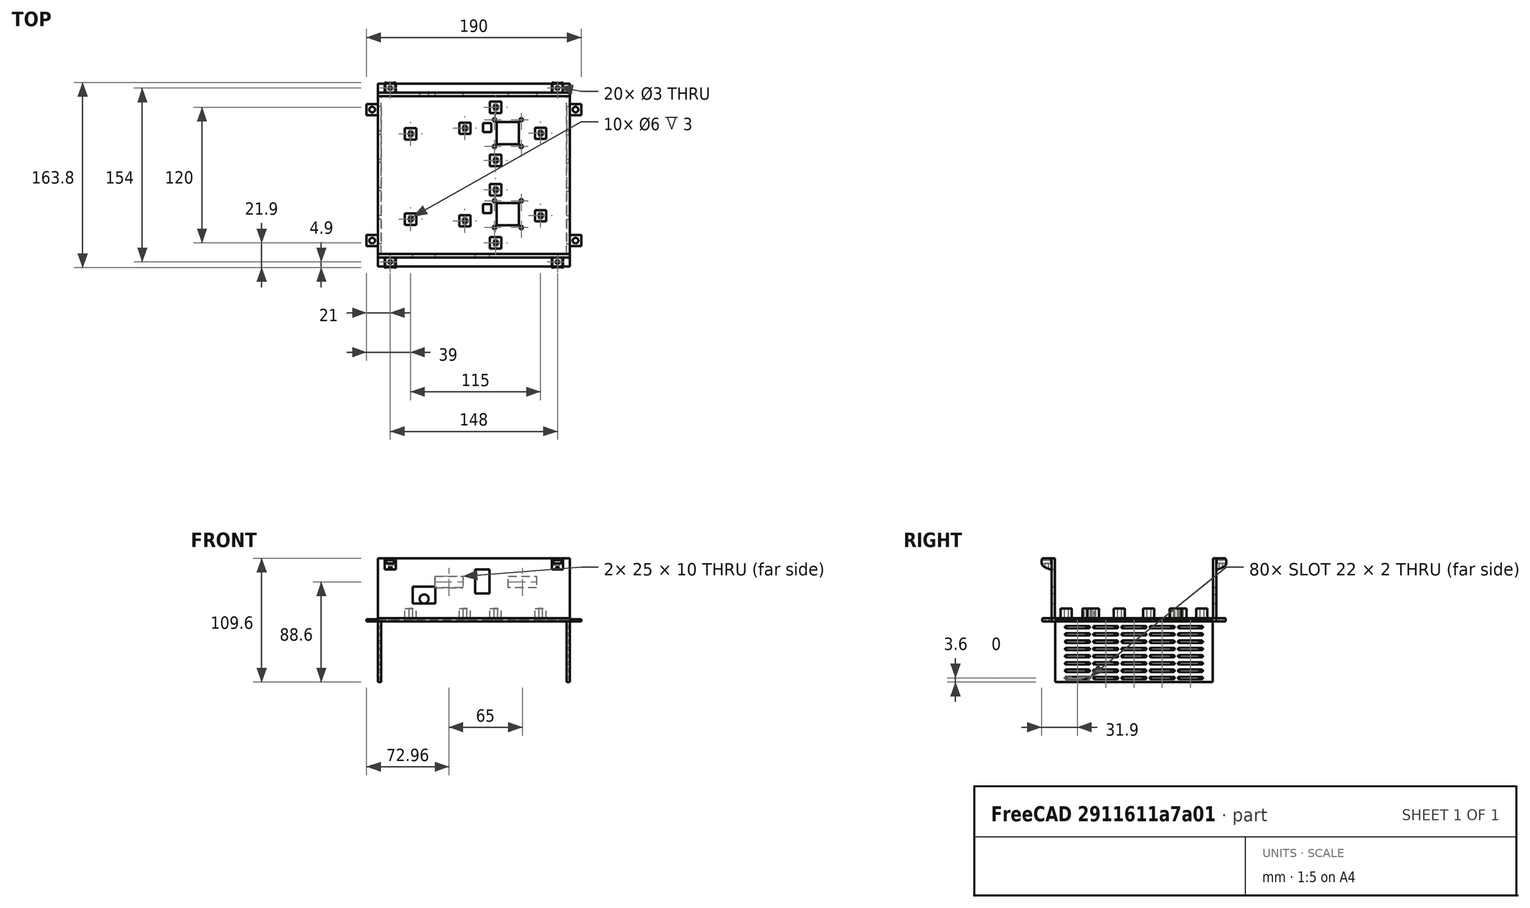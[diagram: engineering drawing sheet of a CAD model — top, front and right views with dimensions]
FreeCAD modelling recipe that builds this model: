
FCSTD DOCUMENT  (FreeCAD 0.21R33771 (Git))
Label: jrobot-electronics-parts
License: All rights reserved
LicenseURL: http://en.wikipedia.org/wiki/All_rights_reserved
objects: PartDesign::CoordinateSystem×24, Sketcher::SketchObject×16, PartDesign::Pocket×7, PartDesign::Pad×5, PartDesign::Mirrored×3, App::DocumentObjectGroup×3, PartDesign::MultiTransform×2, PartDesign::Body×2, App::Part×2, PartDesign::LinearPattern×2, PartDesign::AdditiveLoft×1
note: 75 computed .brp shape members not serialized (recipe doc carries the construction recipe); baked Part::Feature solids carry a one-line shape summary decoded from their .brp

FEATURE [PartDesign::CoordinateSystem] LCS_ElectronicsBox_Lid
  AttacherType = Attacher::AttachEngine3D
  Placement = pos=(0,0,56) rot=(0,0,1;0rad)
FEATURE [PartDesign::CoordinateSystem] LCS_Origin006  label="LCS_ElectronicsBox_Origin"
  AttacherType = Attacher::AttachEngine3D
  MapMode = 2
  Support = -> [X_Axis026]
FEATURE [Sketcher::SketchObject] Sketch034  label="S_ElectronicsBox_HoleLocations"
  FullyConstrained = true
  Support = -> [XY_Plane027]
  sketch-geometry (27):
    g0: LineSegment StartX=-85 StartY=73 StartZ=0 EndX=-85 EndY=-73 EndZ=0
    g1: LineSegment StartX=-85 StartY=-73 StartZ=0 EndX=85 EndY=-73 EndZ=0
    g2: LineSegment StartX=85 StartY=-73 StartZ=0 EndX=85 EndY=73 EndZ=0
    g3: LineSegment StartX=85 StartY=73 StartZ=0 EndX=-85 EndY=73 EndZ=0
    g4: GeomPoint X=0 Y=0 Z=0
    g5: LineSegment StartX=5 StartY=63 StartZ=0 EndX=74 EndY=63 EndZ=0
    g6: LineSegment StartX=74 StartY=63 StartZ=0 EndX=74 EndY=10 EndZ=0
    g7: LineSegment StartX=74 StartY=10 StartZ=0 EndX=5 EndY=10 EndZ=0
    g8: LineSegment StartX=5 StartY=10 StartZ=0 EndX=5 EndY=63 EndZ=0
    g9: LineSegment StartX=5 StartY=-10 StartZ=0 EndX=74 EndY=-10 EndZ=0
    g10: LineSegment StartX=74 StartY=-10 StartZ=0 EndX=74 EndY=-63 EndZ=0
    g11: LineSegment StartX=74 StartY=-63 StartZ=0 EndX=5 EndY=-63 EndZ=0
    g12: LineSegment StartX=5 StartY=-63 StartZ=0 EndX=5 EndY=-10 EndZ=0
    g13: LineSegment StartX=-60 StartY=54 StartZ=0 EndX=-5 EndY=54 EndZ=0
    g14: LineSegment StartX=-5 StartY=54 StartZ=0 EndX=-5 EndY=-54 EndZ=0
    g15: LineSegment StartX=-5 StartY=-54 StartZ=0 EndX=-60 EndY=-54 EndZ=0
    g16: LineSegment StartX=-60 StartY=-54 StartZ=0 EndX=-60 EndY=54 EndZ=0
    g17: GeomPoint X=19.25 Y=60 Z=0
    g18: GeomPoint X=19.25 Y=13 Z=0
    g19: GeomPoint X=19.25 Y=-60 Z=0
    g20: GeomPoint X=19.25 Y=-13 Z=0
    g21: GeomPoint X=59 Y=37 Z=0
    g22: GeomPoint X=59 Y=-36 Z=0
    g23: GeomPoint X=-56 Y=36.5 Z=0
    g24: GeomPoint X=-8 Y=41.5 Z=0
    g25: GeomPoint X=-56 Y=-39 Z=0
    g26: GeomPoint X=-8 Y=-40.5 Z=0
  constraints (70):
    c: Coincident(g0,g1)
    c: Coincident(g1,g2)
    c: Coincident(g2,g3)
    c: Coincident(g3,g0)
    c: Horizontal(g1)
    c: Horizontal(g3)
    c: Vertical(g0)
    c: Vertical(g2)
    c: Symmetric(g1,g0,g4)
    c: Coincident(g4,g-1)
    c: Coincident(g5,g6)
    c: Coincident(g6,g7)
    c: Coincident(g7,g8)
    c: Coincident(g8,g5)
    c: Horizontal(g5)
    c: Horizontal(g7)
    c: Vertical(g6)
    c: Vertical(g8)
    c: DistanceX(g5,g5) = 69
    c: DistanceY(g6,g6) = 53
    c: Coincident(g9,g10)
    c: Coincident(g10,g11)
    c: Coincident(g11,g12)
    c: Coincident(g12,g9)
    c: Horizontal(g9)
    c: Horizontal(g11)
    c: Vertical(g10)
    c: Vertical(g12)
    c: Equal(g7,g9)
    c: Equal(g6,g10)
    c: Vertical(g7,g9)
    c: DistanceY(g9,g7) = 20
    c: DistanceY(g4,g7) = 10
    c: Coincident(g13,g14)
    c: Coincident(g14,g15)
    c: Coincident(g15,g16)
    c: Coincident(g16,g13)
    c: Horizontal(g13)
    c: Horizontal(g15)
    c: Vertical(g16)
    c: DistanceX(g13,g13) = 55
    c: DistanceY(g14,g14) = 108
    c: DistanceX(g13,g4) = 5
    c: DistanceX(g4,g5) = 5
    c: Symmetric(g13,g14,g-1)
    c: DistanceX(g0,g13) = 25
    c: DistanceY(g17,g5) = 3
    c: DistanceY(g7,g18) = 3
    c: DistanceX(g7,g18) = 14.25
    c: Vertical(g18,g17)
    c: DistanceX(g11,g19) = 14.25
    c: DistanceY(g11,g19) = 3
    c: DistanceY(g20,g9) = 3
    c: Vertical(g20,g19)
    c: Vertical(g21,g22)
    c: DistanceY(g21,g5) = 26
    c: DistanceY(g22,g9) = 26
    c: DistanceY(g2,g2) = 146
    c: DistanceY(g25,g23) = 75.5
    c: DistanceX(g15,g25) = 4
    c: DistanceY(g15,g25) = 15
    c: Vertical(g23,g25)
    c: DistanceY(g14,g26) = 13.5
    c: DistanceX(g26,g14) = 3
    c: Vertical(g24,g26)
    c: DistanceY(g26,g24) = 82
    c: DistanceX(g22,g10) = 15
    c: DistanceY(g18,g17) = 47  'HoleYSeparation1'
    c: DistanceY(g18,g21) = 24  'HoleYSeparation0'
    c: DistanceX(g18,g21) = 39.75  'HoleXSeparation'
FEATURE [Sketcher::SketchObject] Sketch033  label="S_ElectronicsBox_Base"
  ExternalGeometry = -> [Sketch034]
  FullyConstrained = true
  MapMode = 5
  Support = -> [XY_Plane027]
  sketch-geometry (24):
    g0: LineSegment StartX=-85 StartY=73 StartZ=0 EndX=-85 EndY=63 EndZ=0
    g1: LineSegment StartX=-85 StartY=-73 StartZ=0 EndX=85 EndY=-73 EndZ=0
    g2: LineSegment StartX=85 StartY=73 StartZ=0 EndX=-85 EndY=73 EndZ=0
    g3: LineSegment StartX=-85 StartY=63 StartZ=0 EndX=-95 EndY=63 EndZ=0
    g4: LineSegment StartX=-95 StartY=63 StartZ=0 EndX=-95 EndY=53 EndZ=0
    g5: LineSegment StartX=-95 StartY=53 StartZ=0 EndX=-85 EndY=53 EndZ=0
    g6: LineSegment StartX=-85 StartY=-53 StartZ=0 EndX=-95 EndY=-53 EndZ=0
    g7: LineSegment StartX=-95 StartY=-53 StartZ=0 EndX=-95 EndY=-63 EndZ=0
    g8: LineSegment StartX=-95 StartY=-63 StartZ=0 EndX=-85 EndY=-63 EndZ=0
    g9: LineSegment StartX=85 StartY=63 StartZ=0 EndX=95 EndY=63 EndZ=0
    g10: LineSegment StartX=95 StartY=63 StartZ=0 EndX=95 EndY=53 EndZ=0
    g11: LineSegment StartX=95 StartY=53 StartZ=0 EndX=85 EndY=53 EndZ=0
    g12: LineSegment StartX=85 StartY=-53 StartZ=0 EndX=95 EndY=-53 EndZ=0
    g13: LineSegment StartX=95 StartY=-53 StartZ=0 EndX=95 EndY=-63 EndZ=0
    g14: LineSegment StartX=95 StartY=-63 StartZ=0 EndX=85 EndY=-63 EndZ=0
    g15: LineSegment StartX=-85 StartY=-63 StartZ=0 EndX=-85 EndY=-73 EndZ=0
    g16: LineSegment StartX=-85 StartY=53 StartZ=0 EndX=-85 EndY=-53 EndZ=0
    g17: LineSegment StartX=85 StartY=-73 StartZ=0 EndX=85 EndY=-63 EndZ=0
    g18: LineSegment StartX=85 StartY=-53 StartZ=0 EndX=85 EndY=53 EndZ=0
    g19: LineSegment StartX=85 StartY=63 StartZ=0 EndX=85 EndY=73 EndZ=0
    g20: Circle CenterX=-90 CenterY=-58 CenterZ=0 NormalX=0 NormalY=0 NormalZ=1 AngleXU=0 Radius=2.5
    g21: Circle CenterX=-90 CenterY=58 CenterZ=0 NormalX=0 NormalY=0 NormalZ=1 AngleXU=0 Radius=2.5
    g22: Circle CenterX=90 CenterY=58 CenterZ=0 NormalX=0 NormalY=0 NormalZ=1 AngleXU=0 Radius=2.5
    g23: Circle CenterX=90 CenterY=-58 CenterZ=0 NormalX=0 NormalY=0 NormalZ=1 AngleXU=0 Radius=2.5
  constraints (70):
    c: Coincident(g2,g0)
    c: Horizontal(g1)
    c: Horizontal(g2)
    c: Vertical(g0)
    c: Symmetric(g1,g0,g-1)
    c: Coincident(g0,g-3)
    c: Coincident(g3,g4)
    c: Coincident(g4,g5)
    c: Horizontal(g3)
    c: Horizontal(g5)
    c: Vertical(g4)
    c: Coincident(g6,g7)
    c: Coincident(g7,g8)
    c: Horizontal(g6)
    c: Horizontal(g8)
    c: Vertical(g7)
    c: PointOnObject(g6,g0)
    c: Coincident(g9,g10)
    c: Coincident(g10,g11)
    c: Horizontal(g9)
    c: Horizontal(g11)
    c: Vertical(g10)
    c: Coincident(g12,g13)
    c: Coincident(g13,g14)
    c: Horizontal(g12)
    c: Horizontal(g14)
    c: Vertical(g13)
    c: Horizontal(g3,g9)
    c: Horizontal(g5,g11)
    c: Horizontal(g12,g6)
    c: Horizontal(g8,g14)
    c: DistanceY(g7,g7) = 10
    c: Equal(g7,g4)
    c: DistanceX(g8,g8) = 10
    c: Equal(g8,g14)
    c: Vertical(g10,g12)
    c: Equal(g5,g8)
    c: DistanceY(g1,g8) = 10
    c: DistanceY(g3,g0) = 10
    c: Coincident(g0,g3)
    c: Vertical(g5,g0)
    c: Coincident(g15,g8)
    c: Coincident(g15,g1)
    c: Vertical(g15)
    c: Vertical(g6,g1)
    c: Coincident(g16,g5)
    c: Coincident(g16,g6)
    c: Coincident(g17,g1)
    c: Coincident(g17,g14)
    c: Vertical(g17)
    c: Coincident(g18,g12)
    c: Coincident(g18,g11)
    c: Vertical(g18)
    c: Coincident(g19,g9)
    c: Coincident(g19,g2)
    c: Vertical(g19)
    c: Vertical(g18,g9)
    c: DistanceX(g0,g2) = 170
    c: Diameter(g20) = 5
    c: DistanceX(g20,g6) = 5
    c: DistanceY(g8,g20) = 5
    c: DistanceY(g21,g0) = 5
    c: DistanceX(g21,g0) = 5
    c: Diameter(g21) = 5
    c: Diameter(g23) = 5
    c: Diameter(g22) = 5
    c: DistanceX(g9,g22) = 5
    c: Horizontal(g21,g22)
    c: Horizontal(g20,g23)
    c: Vertical(g23,g22)
FEATURE [PartDesign::Pad] Pad016  label="PAD_ElectronicsBox_Base"
  Direction = (0,0,1)
  Length = 2
  Length2 = 10
  Profile = -> Sketch033
  ReferenceAxis = -> Sketch033 [N_Axis]
  Type = 0
FEATURE [Sketcher::SketchObject] Sketch035  label="S_ElectronicsBox_HolePads"
  ExternalGeometry = -> [Sketch034]
  FullyConstrained = true
  MapMode = 5
  Placement = pos=(0,0,1.5) rot=(0,0,1;0rad)
  sketch-geometry (50):
    g0: LineSegment StartX=-61 StartY=41.5 StartZ=0 EndX=-61 EndY=31.5 EndZ=0
    g1: LineSegment StartX=-61 StartY=31.5 StartZ=0 EndX=-51 EndY=31.5 EndZ=0
    g2: LineSegment StartX=-51 StartY=31.5 StartZ=0 EndX=-51 EndY=41.5 EndZ=0
    g3: LineSegment StartX=-51 StartY=41.5 StartZ=0 EndX=-61 EndY=41.5 EndZ=0
    g4: GeomPoint X=-56 Y=36.5 Z=0
    g5: LineSegment StartX=-61 StartY=-34 StartZ=0 EndX=-61 EndY=-44 EndZ=0
    g6: LineSegment StartX=-61 StartY=-44 StartZ=0 EndX=-51 EndY=-44 EndZ=0
    g7: LineSegment StartX=-51 StartY=-44 StartZ=0 EndX=-51 EndY=-34 EndZ=0
    g8: LineSegment StartX=-51 StartY=-34 StartZ=0 EndX=-61 EndY=-34 EndZ=0
    g9: GeomPoint X=-56 Y=-39 Z=0
    g10: LineSegment StartX=-13 StartY=46.5 StartZ=0 EndX=-13 EndY=36.5 EndZ=0
    g11: LineSegment StartX=-13 StartY=36.5 StartZ=0 EndX=-3 EndY=36.5 EndZ=0
    g12: LineSegment StartX=-3 StartY=36.5 StartZ=0 EndX=-3 EndY=46.5 EndZ=0
    g13: LineSegment StartX=-3 StartY=46.5 StartZ=0 EndX=-13 EndY=46.5 EndZ=0
    g14: GeomPoint X=-8 Y=41.5 Z=0
    g15: LineSegment StartX=-13 StartY=-35.5 StartZ=0 EndX=-13 EndY=-45.5 EndZ=0
    g16: LineSegment StartX=-13 StartY=-45.5 StartZ=0 EndX=-3 EndY=-45.5 EndZ=0
    g17: LineSegment StartX=-3 StartY=-45.5 StartZ=0 EndX=-3 EndY=-35.5 EndZ=0
    g18: LineSegment StartX=-3 StartY=-35.5 StartZ=0 EndX=-13 EndY=-35.5 EndZ=0
    g19: GeomPoint X=-8 Y=-40.5 Z=0
    g20: LineSegment StartX=14.25 StartY=65 StartZ=0 EndX=14.25 EndY=55 EndZ=0
    g21: LineSegment StartX=14.25 StartY=55 StartZ=0 EndX=24.25 EndY=55 EndZ=0
    g22: LineSegment StartX=24.25 StartY=55 StartZ=0 EndX=24.25 EndY=65 EndZ=0
    g23: LineSegment StartX=24.25 StartY=65 StartZ=0 EndX=14.25 EndY=65 EndZ=0
    g24: GeomPoint X=19.25 Y=60 Z=0
    g25: LineSegment StartX=54 StartY=42 StartZ=0 EndX=54 EndY=32 EndZ=0
    g26: LineSegment StartX=54 StartY=32 StartZ=0 EndX=64 EndY=32 EndZ=0
    g27: LineSegment StartX=64 StartY=32 StartZ=0 EndX=64 EndY=42 EndZ=0
    g28: LineSegment StartX=64 StartY=42 StartZ=0 EndX=54 EndY=42 EndZ=0
    g29: GeomPoint X=59 Y=37 Z=0
    g30: LineSegment StartX=14.25 StartY=18 StartZ=0 EndX=14.25 EndY=8 EndZ=0
    g31: LineSegment StartX=14.25 StartY=8 StartZ=0 EndX=24.25 EndY=8 EndZ=0
    g32: LineSegment StartX=24.25 StartY=8 StartZ=0 EndX=24.25 EndY=18 EndZ=0
    g33: LineSegment StartX=24.25 StartY=18 StartZ=0 EndX=14.25 EndY=18 EndZ=0
    g34: GeomPoint X=19.25 Y=13 Z=0
    g35: LineSegment StartX=14.25 StartY=-8 StartZ=0 EndX=14.25 EndY=-18 EndZ=0
    g36: LineSegment StartX=14.25 StartY=-18 StartZ=0 EndX=24.25 EndY=-18 EndZ=0
    g37: LineSegment StartX=24.25 StartY=-18 StartZ=0 EndX=24.25 EndY=-8 EndZ=0
    g38: LineSegment StartX=24.25 StartY=-8 StartZ=0 EndX=14.25 EndY=-8 EndZ=0
    g39: GeomPoint X=19.25 Y=-13 Z=0
    g40: LineSegment StartX=54 StartY=-31 StartZ=0 EndX=54 EndY=-41 EndZ=0
    g41: LineSegment StartX=54 StartY=-41 StartZ=0 EndX=64 EndY=-41 EndZ=0
    g42: LineSegment StartX=64 StartY=-41 StartZ=0 EndX=64 EndY=-31 EndZ=0
    g43: LineSegment StartX=64 StartY=-31 StartZ=0 EndX=54 EndY=-31 EndZ=0
    g44: GeomPoint X=59 Y=-36 Z=0
    g45: LineSegment StartX=14.25 StartY=-55 StartZ=0 EndX=14.25 EndY=-65 EndZ=0
    g46: LineSegment StartX=14.25 StartY=-65 StartZ=0 EndX=24.25 EndY=-65 EndZ=0
    g47: LineSegment StartX=24.25 StartY=-65 StartZ=0 EndX=24.25 EndY=-55 EndZ=0
    g48: LineSegment StartX=24.25 StartY=-55 StartZ=0 EndX=14.25 EndY=-55 EndZ=0
    g49: GeomPoint X=19.25 Y=-60 Z=0
  constraints (120):
    c: Coincident(g0,g1)
    c: Coincident(g1,g2)
    c: Coincident(g2,g3)
    c: Coincident(g3,g0)
    c: Horizontal(g1)
    c: Horizontal(g3)
    c: Vertical(g0)
    c: Vertical(g2)
    c: Symmetric(g1,g0,g4)
    c: Coincident(g5,g6)
    c: Coincident(g6,g7)
    c: Coincident(g7,g8)
    c: Coincident(g8,g5)
    c: Horizontal(g6)
    c: Horizontal(g8)
    c: Vertical(g5)
    c: Vertical(g7)
    c: Symmetric(g6,g5,g9)
    c: Coincident(g10,g11)
    c: Coincident(g11,g12)
    c: Coincident(g12,g13)
    c: Coincident(g13,g10)
    c: Horizontal(g11)
    c: Horizontal(g13)
    c: Vertical(g10)
    c: Vertical(g12)
    c: Symmetric(g11,g10,g14)
    c: Coincident(g15,g16)
    c: Coincident(g16,g17)
    c: Coincident(g17,g18)
    c: Coincident(g18,g15)
    c: Horizontal(g16)
    c: Horizontal(g18)
    c: Vertical(g15)
    c: Vertical(g17)
    c: Symmetric(g16,g15,g19)
    c: Coincident(g20,g21)
    c: Coincident(g21,g22)
    c: Coincident(g22,g23)
    c: Coincident(g23,g20)
    c: Horizontal(g21)
    c: Horizontal(g23)
    c: Vertical(g20)
    c: Vertical(g22)
    c: Symmetric(g21,g20,g24)
    c: Coincident(g25,g26)
    c: Coincident(g26,g27)
    c: Coincident(g27,g28)
    c: Coincident(g28,g25)
    c: Horizontal(g26)
    c: Horizontal(g28)
    c: Vertical(g25)
    c: Vertical(g27)
    c: Symmetric(g26,g25,g29)
    c: Coincident(g30,g31)
    c: Coincident(g31,g32)
    c: Coincident(g32,g33)
    c: Coincident(g33,g30)
    c: Horizontal(g31)
    c: Horizontal(g33)
    c: Vertical(g30)
    c: Vertical(g32)
    c: Symmetric(g31,g30,g34)
    c: Coincident(g35,g36)
    c: Coincident(g36,g37)
    c: Coincident(g37,g38)
    c: Coincident(g38,g35)
    c: Horizontal(g36)
    c: Horizontal(g38)
    c: Vertical(g35)
    c: Vertical(g37)
    c: Symmetric(g36,g35,g39)
    c: Coincident(g40,g41)
    c: Coincident(g41,g42)
    c: Coincident(g42,g43)
    c: Coincident(g43,g40)
    c: Horizontal(g41)
    c: Horizontal(g43)
    c: Vertical(g40)
    c: Vertical(g42)
    c: Symmetric(g41,g40,g44)
    c: Coincident(g45,g46)
    c: Coincident(g46,g47)
    c: Coincident(g47,g48)
    c: Coincident(g48,g45)
    c: Horizontal(g46)
    c: Horizontal(g48)
    c: Vertical(g45)
    c: Vertical(g47)
    c: Symmetric(g46,g45,g49)
    c: Coincident(g4,g-3)
    c: Coincident(g9,g-12)
    c: Coincident(g19,g-9)
    c: Coincident(g14,g-4)
    c: Coincident(g24,g-11)
    c: Coincident(g29,g-6)
    c: Coincident(g34,g-5)
    c: Coincident(g39,g-10)
    c: Coincident(g44,g-7)
    c: Coincident(g49,g-8)
    c: Equal(g3,g2)
    c: Equal(g8,g7)
    c: Equal(g18,g17)
    c: Equal(g13,g12)
    c: Equal(g33,g32)
    c: Equal(g38,g37)
    c: Equal(g48,g47)
    c: Equal(g43,g42)
    c: Equal(g28,g27)
    c: Equal(g23,g22)
    c: Equal(g3,g8)
    c: Equal(g3,g13)
    c: Equal(g13,g23)
    c: Equal(g23,g28)
    c: Equal(g28,g33)
    c: Equal(g33,g38)
    c: Equal(g38,g48)
    c: Equal(g18,g8)
    c: Equal(g48,g43)
    c: DistanceX(g3,g3) = 10
FEATURE [Sketcher::SketchObject] Sketch036  label="S_ElectronicsBox_Holes"
  AttachmentOffset = pos=(2,0,0) rot=(0,0,1;0rad)
  ExternalGeometry = -> [Sketch034]
  FullyConstrained = true
  MapMode = 5
  Placement = pos=(2,0,0) rot=(1,0,0;3.14159rad)
  sketch-geometry (10):
    g0: Circle CenterX=-58 CenterY=39 CenterZ=0 NormalX=0 NormalY=0 NormalZ=1 AngleXU=0 Radius=1.75
    g1: Circle CenterX=-10 CenterY=40.5 CenterZ=0 NormalX=0 NormalY=0 NormalZ=1 AngleXU=0 Radius=1.75
    g2: Circle CenterX=-10 CenterY=-41.5 CenterZ=0 NormalX=0 NormalY=0 NormalZ=1 AngleXU=0 Radius=1.75
    g3: Circle CenterX=-58 CenterY=-36.5 CenterZ=0 NormalX=0 NormalY=0 NormalZ=1 AngleXU=0 Radius=1.75
    g4: Circle CenterX=17.25 CenterY=13 CenterZ=0 NormalX=0 NormalY=0 NormalZ=1 AngleXU=0 Radius=1.75
    g5: Circle CenterX=17.25 CenterY=60 CenterZ=0 NormalX=0 NormalY=0 NormalZ=1 AngleXU=0 Radius=1.75
    g6: Circle CenterX=57 CenterY=36 CenterZ=0 NormalX=0 NormalY=0 NormalZ=1 AngleXU=0 Radius=1.75
    g7: Circle CenterX=57 CenterY=-37 CenterZ=0 NormalX=0 NormalY=0 NormalZ=1 AngleXU=0 Radius=1.75
    g8: Circle CenterX=17.25 CenterY=-13 CenterZ=0 NormalX=0 NormalY=0 NormalZ=1 AngleXU=0 Radius=1.75
    g9: Circle CenterX=17.25 CenterY=-60 CenterZ=0 NormalX=0 NormalY=0 NormalZ=1 AngleXU=0 Radius=1.75
  constraints (20):
    c: Coincident(g0,g-3)
    c: Coincident(g1,g-4)
    c: Coincident(g2,g-5)
    c: Coincident(g3,g-6)
    c: Coincident(g4,g-12)
    c: Coincident(g5,g-11)
    c: Coincident(g6,g-10)
    c: Coincident(g7,g-9)
    c: Coincident(g8,g-8)
    c: Coincident(g9,g-7)
    c: Equal(g0,g1)
    c: Equal(g1,g2)
    c: Equal(g2,g3)
    c: Equal(g3,g8)
    c: Equal(g8,g9)
    c: Equal(g9,g7)
    c: Equal(g7,g4)
    c: Equal(g4,g6)
    c: Equal(g6,g5)
    c: Diameter(g0) = 3.5
FEATURE [Sketcher::SketchObject] Sketch037  label="S_ElectronicsBox_BoltIndent"
  ExternalGeometry = -> [Sketch034]
  FullyConstrained = true
  MapMode = 5
  Placement = pos=(0,0,0) rot=(1,0,0;3.14159rad)
  sketch-geometry (10):
    g0: Circle CenterX=-56 CenterY=39 CenterZ=0 NormalX=0 NormalY=0 NormalZ=1 AngleXU=0 Radius=3
    g1: Circle CenterX=-8 CenterY=40.5 CenterZ=0 NormalX=0 NormalY=0 NormalZ=1 AngleXU=0 Radius=3
    g2: Circle CenterX=-8 CenterY=-41.5 CenterZ=0 NormalX=0 NormalY=0 NormalZ=1 AngleXU=0 Radius=3
    g3: Circle CenterX=-56 CenterY=-36.5 CenterZ=0 NormalX=0 NormalY=0 NormalZ=1 AngleXU=0 Radius=3
    g4: Circle CenterX=19.25 CenterY=13 CenterZ=0 NormalX=0 NormalY=0 NormalZ=1 AngleXU=0 Radius=3
    g5: Circle CenterX=19.25 CenterY=60 CenterZ=0 NormalX=0 NormalY=0 NormalZ=1 AngleXU=0 Radius=3
    g6: Circle CenterX=59 CenterY=36 CenterZ=0 NormalX=0 NormalY=0 NormalZ=1 AngleXU=0 Radius=3
    g7: Circle CenterX=59 CenterY=-37 CenterZ=0 NormalX=0 NormalY=0 NormalZ=1 AngleXU=0 Radius=3
    g8: Circle CenterX=19.25 CenterY=-13 CenterZ=0 NormalX=0 NormalY=0 NormalZ=1 AngleXU=0 Radius=3
    g9: Circle CenterX=19.25 CenterY=-60 CenterZ=0 NormalX=0 NormalY=0 NormalZ=1 AngleXU=0 Radius=3
  constraints (20):
    c: Coincident(g0,g-3)
    c: Coincident(g1,g-4)
    c: Coincident(g2,g-5)
    c: Coincident(g3,g-6)
    c: Coincident(g4,g-12)
    c: Coincident(g5,g-11)
    c: Coincident(g6,g-10)
    c: Coincident(g7,g-9)
    c: Coincident(g8,g-8)
    c: Coincident(g9,g-7)
    c: Equal(g0,g1)
    c: Equal(g1,g2)
    c: Equal(g2,g3)
    c: Equal(g3,g8)
    c: Equal(g8,g9)
    c: Equal(g9,g7)
    c: Equal(g7,g4)
    c: Equal(g4,g6)
    c: Equal(g6,g5)
    c: Diameter(g0) = 6
FEATURE [Sketcher::SketchObject] Sketch038  label="S_ElectronicsBox_Switches"
  FullyConstrained = true
  MapMode = 5
  Placement = pos=(0,-73,0) rot=(1,0,0;1.5708rad)
  sketch-geometry (10):
    g0: LineSegment StartX=1.16 StartY=46 StartZ=0 EndX=13.66 EndY=46 EndZ=0
    g1: LineSegment StartX=13.66 StartY=46 StartZ=0 EndX=13.66 EndY=25 EndZ=0
    g2: LineSegment StartX=13.66 StartY=25 StartZ=0 EndX=1.16 EndY=25 EndZ=0
    g3: LineSegment StartX=1.16 StartY=25 StartZ=0 EndX=1.16 EndY=46 EndZ=0
    g4: LineSegment StartX=-54 StartY=31 StartZ=0 EndX=-34 EndY=31 EndZ=0
    g5: LineSegment StartX=-34 StartY=31 StartZ=0 EndX=-34 EndY=16 EndZ=0
    g6: LineSegment StartX=-34 StartY=16 StartZ=0 EndX=-54 EndY=16 EndZ=0
    g7: LineSegment StartX=-54 StartY=16 StartZ=0 EndX=-54 EndY=31 EndZ=0
    g8: GeomPoint X=-44 Y=23.5 Z=0
    g9: GeomPoint X=7.41 Y=35.5 Z=0
  constraints (30):
    c: Coincident(g0,g1)
    c: Coincident(g1,g2)
    c: Coincident(g2,g3)
    c: Coincident(g3,g0)
    c: Horizontal(g0)
    c: Horizontal(g2)
    c: Vertical(g1)
    c: Vertical(g3)
    c: DistanceX(g0,g0) = 12.5
    c: DistanceY(g3,g3) = 21
    c: Coincident(g4,g5)
    c: Coincident(g5,g6)
    c: Coincident(g6,g7)
    c: Coincident(g7,g4)
    c: Horizontal(g4)
    c: Horizontal(g6)
    c: Vertical(g5)
    c: Vertical(g7)
    c: DistanceY(g-1,g5) = 16
    c: DistanceY(g6,g4) = 15
    c: DistanceX(g4,g4) = 20
    c: DistanceX(g5,g-1) = 34
    c: DistanceX(g-1,g2) = 1.16
    c: DistanceY(g-1,g1) = 25
    c: Symmetric(g1,g0,g9)
    c: Symmetric(g4,g5,g8)
    c: DistanceY(g-1,g8) = 23.5  'USBY'
    c: DistanceX(g8,g-1) = 44  'USBX'
    c: DistanceY(g-1,g9) = 35.5  'SwitchY'
    c: DistanceX(g-1,g9) = 7.41  'SwitchX'
FEATURE [Sketcher::SketchObject] Sketch039  label="S_ElectronicsBox_WallsBase"
  ExternalGeometry = -> [Sketch034,Sketch033]
  FullyConstrained = true
  MapMode = 2
  Support = -> [Pad016]
  sketch-geometry (8):
    g0: LineSegment StartX=-85 StartY=73 StartZ=0 EndX=85 EndY=73 EndZ=0
    g1: LineSegment StartX=85 StartY=73 StartZ=0 EndX=85 EndY=70 EndZ=0
    g2: LineSegment StartX=85 StartY=70 StartZ=0 EndX=-85 EndY=70 EndZ=0
    g3: LineSegment StartX=-85 StartY=70 StartZ=0 EndX=-85 EndY=73 EndZ=0
    g4: LineSegment StartX=-85 StartY=-73 StartZ=0 EndX=85 EndY=-73 EndZ=0
    g5: LineSegment StartX=85 StartY=-73 StartZ=0 EndX=85 EndY=-70 EndZ=0
    g6: LineSegment StartX=85 StartY=-70 StartZ=0 EndX=-85 EndY=-70 EndZ=0
    g7: LineSegment StartX=-85 StartY=-70 StartZ=0 EndX=-85 EndY=-73 EndZ=0
  constraints (20):
    c: Coincident(g0,g1)
    c: Coincident(g1,g2)
    c: Coincident(g2,g3)
    c: Coincident(g3,g0)
    c: Horizontal(g2)
    c: Vertical(g1)
    c: Vertical(g3)
    c: Coincident(g0,g-3)
    c: Coincident(g0,g-4)
    c: DistanceY(g3,g3) = 3
    c: Coincident(g4,g5)
    c: Coincident(g5,g6)
    c: Coincident(g6,g7)
    c: Coincident(g7,g4)
    c: Horizontal(g6)
    c: Vertical(g5)
    c: Vertical(g7)
    c: Coincident(g4,g-6)
    c: Coincident(g4,g-5)
    c: DistanceY(g7,g7) = 3
FEATURE [PartDesign::Pad] Pad017  label="PAD_ElectronicsBoxWalls"
  BaseFeature = -> Pad016
  Direction = (0,0,1)
  Length = 56
  Length2 = 10
  Profile = -> Sketch039
  ReferenceAxis = -> Sketch039 [N_Axis]
  Type = 0
FEATURE [Sketcher::SketchObject] Sketch041  label="S_ElectronicsBox_TopTabBase"
  FullyConstrained = false
  MapMode = 2
  Placement = pos=(0,0,46) rot=(0,0,1;0rad)
  sketch-geometry (4):
    g0: LineSegment StartX=-79 StartY=72.75 StartZ=0 EndX=-69 EndY=72.75 EndZ=0
    g1: LineSegment StartX=-69 StartY=72.75 StartZ=0 EndX=-69 EndY=73 EndZ=0
    g2: LineSegment StartX=-69 StartY=73 StartZ=0 EndX=-79 EndY=73 EndZ=0
    g3: LineSegment StartX=-79 StartY=73 StartZ=0 EndX=-79 EndY=72.75 EndZ=0
  constraints (9):
    c: Coincident(g0,g1)
    c: Coincident(g1,g2)
    c: Coincident(g2,g3)
    c: Coincident(g3,g0)
    c: Horizontal(g0)
    c: Horizontal(g2)
    c: Vertical(g1)
    c: Vertical(g3)
    c: DistanceX(g0,g0) = 10
FEATURE [Sketcher::SketchObject] Sketch042  label="S_ElectronicsBox_TopTabTop"
  ExternalGeometry = -> [Sketch039,Sketch033]
  FullyConstrained = true
  MapMode = 2
  Placement = pos=(0,0,56) rot=(0,0,1;0rad)
  sketch-geometry (4):
    g0: LineSegment StartX=-79 StartY=81 StartZ=0 EndX=-69 EndY=81 EndZ=0
    g1: LineSegment StartX=-69 StartY=81 StartZ=0 EndX=-69 EndY=73 EndZ=0
    g2: LineSegment StartX=-69 StartY=73 StartZ=0 EndX=-79 EndY=73 EndZ=0
    g3: LineSegment StartX=-79 StartY=73 StartZ=0 EndX=-79 EndY=81 EndZ=0
  constraints (12):
    c: Coincident(g0,g1)
    c: Coincident(g1,g2)
    c: Coincident(g2,g3)
    c: Coincident(g3,g0)
    c: Horizontal(g0)
    c: Horizontal(g2)
    c: Vertical(g1)
    c: Vertical(g3)
    c: DistanceX(g0,g0) = 10
    c: DistanceX(g-4,g0) = 6
    c: DistanceY(g-4,g0) = 8
    c: Horizontal(g2,g-4)
FEATURE [Sketcher::SketchObject] Sketch040  label="S_ElectronicsBox_WallsTopHoles"
  ExternalGeometry = -> [Sketch042]
  FullyConstrained = true
  MapMode = 5
  Placement = pos=(0,0,59) rot=(0,0,1;0rad)
  sketch-geometry (5):
    g0: Circle CenterX=-74 CenterY=77 CenterZ=0 NormalX=0 NormalY=0 NormalZ=1 AngleXU=0 Radius=1.5
    g1: LineSegment StartX=-79 StartY=81 StartZ=0 EndX=-79 EndY=77 EndZ=0
    g2: LineSegment StartX=-79 StartY=77 StartZ=0 EndX=-79 EndY=73 EndZ=0
    g3: LineSegment StartX=-79 StartY=81 StartZ=0 EndX=-74 EndY=81 EndZ=0
    g4: LineSegment StartX=-74 StartY=81 StartZ=0 EndX=-69 EndY=81 EndZ=0
  constraints (13):
    c: Diameter(g0) = 3
    c: Coincident(g1,g-3)
    c: Vertical(g1)
    c: Coincident(g2,g1)
    c: Coincident(g2,g-5)
    c: Coincident(g3,g1)
    c: Horizontal(g3)
    c: Coincident(g4,g3)
    c: Coincident(g4,g-4)
    c: Equal(g3,g4)
    c: Equal(g1,g2)
    c: Vertical(g0,g3)
    c: Horizontal(g1,g0)
FEATURE [Sketcher::SketchObject] Sketch043  label="S_ElectronicsBox_TopTabMid"
  AttachmentOffset = pos=(0,0,-6) rot=(0,0,1;0rad)
  ExternalGeometry = -> [Sketch039,Sketch033]
  FullyConstrained = true
  MapMode = 2
  Placement = pos=(0,0,50) rot=(0,0,1;0rad)
  sketch-geometry (4):
    g0: LineSegment StartX=-79 StartY=81 StartZ=0 EndX=-69 EndY=81 EndZ=0
    g1: LineSegment StartX=-69 StartY=81 StartZ=0 EndX=-69 EndY=73 EndZ=0
    g2: LineSegment StartX=-69 StartY=73 StartZ=0 EndX=-79 EndY=73 EndZ=0
    g3: LineSegment StartX=-79 StartY=73 StartZ=0 EndX=-79 EndY=81 EndZ=0
  constraints (12):
    c: Coincident(g3,g0)
    c: Horizontal(g0)
    c: Horizontal(g2)
    c: Vertical(g1)
    c: Vertical(g3)
    c: DistanceX(g0,g0) = 10
    c: DistanceX(g-4,g0) = 6
    c: DistanceY(g-4,g0) = 8
    c: Coincident(g1,g2)
    c: Coincident(g2,g3)
    c: Coincident(g0,g1)
    c: Horizontal(g2,g-4)
FEATURE [PartDesign::AdditiveLoft] AdditiveLoft  label="LOFT_ElectronicsBox_Tabs"
  BaseFeature = -> Pad017
  Closed = false
  Profile = -> Sketch041
  Ruled = false
  Sections = -> [Sketch043,Sketch042]
FEATURE [PartDesign::Pocket] Pocket014  label="POCKET_ElectronicsBox_WallsTopHoles"
  BaseFeature = -> AdditiveLoft
  Direction = (0,0,-1)
  Length = 20
  Length2 = 5
  Profile = -> Sketch040
  ReferenceAxis = -> Sketch040 [N_Axis]
  Type = 0
FEATURE [Sketcher::SketchObject] Sketch045  label="S_ElectronicsBox_BackWires"
  FullyConstrained = false
  MapMode = 5
  Placement = pos=(0,73,0) rot=(0,0.707107,0.707107;3.14159rad)
  sketch-geometry (9):
    g0: LineSegment StartX=-55.46 StartY=40 StartZ=0 EndX=-30.46 EndY=40 EndZ=0
    g1: LineSegment StartX=-30.46 StartY=40 StartZ=0 EndX=-30.46 EndY=30 EndZ=0
    g2: LineSegment StartX=-30.46 StartY=30 StartZ=0 EndX=-55.46 EndY=30 EndZ=0
    g3: LineSegment StartX=-55.46 StartY=30 StartZ=0 EndX=-55.46 EndY=40 EndZ=0
    g4: LineSegment StartX=9.54003 StartY=40 StartZ=0 EndX=34.54 EndY=40 EndZ=0
    g5: LineSegment StartX=34.54 StartY=40 StartZ=0 EndX=34.54 EndY=30 EndZ=0
    g6: LineSegment StartX=34.54 StartY=30 StartZ=0 EndX=9.54003 EndY=30 EndZ=0
    g7: LineSegment StartX=9.54003 StartY=30 StartZ=0 EndX=9.54003 EndY=40 EndZ=0
    g8: Circle CenterX=44 CenterY=20 CenterZ=0 NormalX=0 NormalY=0 NormalZ=1 AngleXU=0 Radius=4
  constraints (26):
    c: Coincident(g0,g1)
    c: Coincident(g1,g2)
    c: Coincident(g2,g3)
    c: Coincident(g3,g0)
    c: Horizontal(g0)
    c: Horizontal(g2)
    c: Vertical(g1)
    c: Vertical(g3)
    c: Coincident(g4,g5)
    c: Coincident(g5,g6)
    c: Coincident(g6,g7)
    c: Coincident(g7,g4)
    c: Horizontal(g4)
    c: Horizontal(g6)
    c: Vertical(g5)
    c: Vertical(g7)
    c: Equal(g1,g7)
    c: Equal(g0,g4)
    c: DistanceY(g-1,g1) = 30
    c: DistanceX(g0,g0) = 25
    c: DistanceY(g1,g1) = 10
    c: DistanceX(g0,g4) = 40
    c: Diameter(g8) = 8
    c: Horizontal(g0,g4)
    c: DistanceY(g-1,g8) = 20  'PowerY'
    c: DistanceX(g-1,g8) = 44  'PowerX'
FEATURE [PartDesign::CoordinateSystem] LCS_Origin007  label="LCS_ElectronicsBox_Cover"
  AttacherType = Attacher::AttachEngine3D
  MapMode = 2
  Support = -> [X_Axis028]
FEATURE [Sketcher::SketchObject] Sketch046  label="S_ElectronicsBox_Cover"
  FullyConstrained = true
  MapMode = 5
  Support = -> [XY_Plane029]
  sketch-geometry (33):
    g0: LineSegment StartX=-85 StartY=-81 StartZ=0 EndX=-85 EndY=81 EndZ=0
    g1: LineSegment StartX=-85 StartY=81 StartZ=0 EndX=85 EndY=81 EndZ=0
    g2: LineSegment StartX=85 StartY=81 StartZ=0 EndX=85 EndY=-81 EndZ=0
    g3: LineSegment StartX=85 StartY=-81 StartZ=0 EndX=-85 EndY=-81 EndZ=0
    g4: GeomPoint X=0 Y=0 Z=0
    g5: Circle CenterX=-74 CenterY=77 CenterZ=0 NormalX=0 NormalY=0 NormalZ=1 AngleXU=0 Radius=1.5
    g6: Circle CenterX=74 CenterY=77 CenterZ=0 NormalX=0 NormalY=0 NormalZ=1 AngleXU=0 Radius=1.5
    g7: Circle CenterX=74 CenterY=-77 CenterZ=0 NormalX=0 NormalY=0 NormalZ=1 AngleXU=0 Radius=1.5
    g8: Circle CenterX=-74 CenterY=-77 CenterZ=0 NormalX=0 NormalY=0 NormalZ=1 AngleXU=0 Radius=1.5
    g9: LineSegment StartX=20.25 StartY=47 StartZ=0 EndX=40 EndY=47 EndZ=0
    g10: LineSegment StartX=40 StartY=47 StartZ=0 EndX=40 EndY=27.25 EndZ=0
    g11: LineSegment StartX=40 StartY=27.25 StartZ=0 EndX=20.25 EndY=27.25 EndZ=0
    g12: LineSegment StartX=20.25 StartY=27.25 StartZ=0 EndX=20.25 EndY=47 EndZ=0
    g13: Circle CenterX=18.25 CenterY=49 CenterZ=0 NormalX=0 NormalY=0 NormalZ=1 AngleXU=0 Radius=1.5
    g14: Circle CenterX=42 CenterY=49 CenterZ=0 NormalX=0 NormalY=0 NormalZ=1 AngleXU=0 Radius=1.5
    g15: Circle CenterX=42 CenterY=25.25 CenterZ=0 NormalX=0 NormalY=0 NormalZ=1 AngleXU=0 Radius=1.5
    g16: Circle CenterX=18.25 CenterY=25.25 CenterZ=0 NormalX=0 NormalY=0 NormalZ=1 AngleXU=0 Radius=1.5
    g17: Circle CenterX=18.25 CenterY=-22.75 CenterZ=0 NormalX=0 NormalY=0 NormalZ=1 AngleXU=0 Radius=1.5
    g18: Circle CenterX=42 CenterY=-22.75 CenterZ=0 NormalX=0 NormalY=0 NormalZ=1 AngleXU=0 Radius=1.5
    g19: Circle CenterX=18.25 CenterY=-46.5 CenterZ=0 NormalX=0 NormalY=0 NormalZ=1 AngleXU=0 Radius=1.5
    g20: Circle CenterX=42 CenterY=-46.5 CenterZ=0 NormalX=0 NormalY=0 NormalZ=1 AngleXU=0 Radius=1.5
    g21: LineSegment StartX=20.25 StartY=-24.75 StartZ=0 EndX=40 EndY=-24.75 EndZ=0
    g22: LineSegment StartX=40 StartY=-24.75 StartZ=0 EndX=40 EndY=-44.5 EndZ=0
    g23: LineSegment StartX=40 StartY=-44.5 StartZ=0 EndX=20.25 EndY=-44.5 EndZ=0
    g24: LineSegment StartX=20.25 StartY=-44.5 StartZ=0 EndX=20.25 EndY=-24.75 EndZ=0
    g25: LineSegment StartX=15.25 StartY=46 StartZ=0 EndX=8.25 EndY=46 EndZ=0
    g26: LineSegment StartX=8.25 StartY=46 StartZ=0 EndX=8.25 EndY=38 EndZ=0
    g27: LineSegment StartX=8.25 StartY=38 StartZ=0 EndX=15.25 EndY=38 EndZ=0
    g28: LineSegment StartX=15.25 StartY=38 StartZ=0 EndX=15.25 EndY=46 EndZ=0
    g29: LineSegment StartX=15.25 StartY=-25.75 StartZ=0 EndX=8.25 EndY=-25.75 EndZ=0
    g30: LineSegment StartX=8.25 StartY=-25.75 StartZ=0 EndX=8.25 EndY=-33.75 EndZ=0
    g31: LineSegment StartX=8.25 StartY=-33.75 StartZ=0 EndX=15.25 EndY=-33.75 EndZ=0
    g32: LineSegment StartX=15.25 StartY=-33.75 StartZ=0 EndX=15.25 EndY=-25.75 EndZ=0
  constraints (96):
    c: Coincident(g0,g1)
    c: Coincident(g1,g2)
    c: Coincident(g2,g3)
    c: Coincident(g3,g0)
    c: Horizontal(g1)
    c: Horizontal(g3)
    c: Vertical(g0)
    c: Vertical(g2)
    c: Symmetric(g1,g0,g4)
    c: Coincident(g4,g-1)
    c: DistanceY(g0,g0) = 162
    c: DistanceX(g1,g1) = 170
    c: Equal(g5,g6)
    c: Equal(g6,g8)
    c: Equal(g8,g7)
    c: Diameter(g5) = 3
    c: Horizontal(g5,g6)
    c: Vertical(g5,g8)
    c: Vertical(g7,g6)
    c: DistanceX(g0,g5) = 11
    c: DistanceY(g5,g0) = 4
    c: Horizontal(g7,g8)
    c: DistanceX(g5,g6) = 148
    c: DistanceY(g0,g8) = 4
    c: Coincident(g9,g10)
    c: Coincident(g10,g11)
    c: Coincident(g11,g12)
    c: Coincident(g12,g9)
    c: Horizontal(g9)
    c: Horizontal(g11)
    c: Vertical(g10)
    c: Vertical(g12)
    c: Diameter(g13) = 3
    c: Equal(g13,g14)
    c: Equal(g14,g15)
    c: Equal(g15,g16)
    c: DistanceX(g13,g14) = 23.75
    c: Horizontal(g14,g13)
    c: Vertical(g13,g16)
    c: Horizontal(g16,g15)
    c: Vertical(g14,g15)
    c: DistanceY(g16,g13) = 23.75
    c: DistanceX(g9,g14) = 2
    c: DistanceX(g13,g9) = 2
    c: DistanceY(g9,g13) = 2
    c: DistanceY(g16,g11) = 2
    c: Equal(g17,g18)
    c: Equal(g18,g20)
    c: Equal(g20,g19)
    c: Equal(g19,g16)
    c: Horizontal(g18,g17)
    c: Horizontal(g19,g20)
    c: Vertical(g17,g19)
    c: Vertical(g18,g20)
    c: DistanceY(g19,g17) = 23.75
    c: DistanceX(g17,g18) = 23.75
    c: Coincident(g21,g22)
    c: Coincident(g22,g23)
    c: Coincident(g23,g24)
    c: Coincident(g24,g21)
    c: Horizontal(g21)
    c: Horizontal(g23)
    c: Vertical(g22)
    c: Vertical(g24)
    c: DistanceX(g17,g21) = 2
    c: DistanceX(g21,g18) = 2
    c: DistanceY(g21,g17) = 2
    c: DistanceY(g19,g23) = 2
    c: Vertical(g16,g17)
    c: DistanceY(g14,g1) = 32
    c: DistanceY(g18,g15) = 48
    c: DistanceX(g20,g2) = 43
    c: Coincident(g25,g26)
    c: Coincident(g26,g27)
    c: Coincident(g27,g28)
    c: Coincident(g28,g25)
    c: Horizontal(g25)
    c: Horizontal(g27)
    c: Vertical(g26)
    c: Vertical(g28)
    c: Coincident(g29,g30)
    c: Coincident(g30,g31)
    c: Coincident(g31,g32)
    c: Coincident(g32,g29)
    c: Horizontal(g29)
    c: Horizontal(g31)
    c: Vertical(g30)
    c: Vertical(g32)
    c: DistanceY(g26,g26) = 8
    c: DistanceX(g25,g25) = 7
    c: DistanceY(g25,g13) = 3
    c: DistanceX(g25,g13) = 3
    c: DistanceX(g29,g29) = 7
    c: DistanceY(g30,g30) = 8
    c: DistanceY(g29,g17) = 3
    c: DistanceX(g29,g17) = 3
FEATURE [PartDesign::Pad] Pad019  label="PAD_ElectronicsBox_Cover"
  Direction = (0,0,1)
  Length = 3
  Length2 = 10
  Profile = -> Sketch046
  ReferenceAxis = -> Sketch046 [N_Axis]
  Type = 0
FEATURE [Sketcher::SketchObject] Sketch047  label="S_ElectronicsBox_NutInset"
  AttachmentOffset = pos=(0,0,-83) rot=(0,0,1;0rad)
  ExternalGeometry = -> [Sketch042]
  FullyConstrained = true
  MapMode = 5
  Placement = pos=(0,83,1.84e-14) rot=(1,0,0;1.5708rad)
  Support = -> [XZ_Plane027]
  sketch-geometry (6):
    g0: LineSegment StartX=-77.5 StartY=54.5 StartZ=0 EndX=-70.5 EndY=54.5 EndZ=0
    g1: LineSegment StartX=-70.5 StartY=54.5 StartZ=0 EndX=-70.5 EndY=51.5 EndZ=0
    g2: LineSegment StartX=-70.5 StartY=51.5 StartZ=0 EndX=-77.5 EndY=51.5 EndZ=0
    g3: LineSegment StartX=-77.5 StartY=51.5 StartZ=0 EndX=-77.5 EndY=54.5 EndZ=0
    g4: LineSegment StartX=-79 StartY=56 StartZ=0 EndX=-77.5 EndY=54.5 EndZ=0
    g5: LineSegment StartX=-69 StartY=56 StartZ=0 EndX=-70.5 EndY=54.5 EndZ=0
  constraints (16):
    c: Coincident(g0,g1)
    c: Coincident(g1,g2)
    c: Coincident(g2,g3)
    c: Coincident(g3,g0)
    c: Horizontal(g0)
    c: Horizontal(g2)
    c: Vertical(g1)
    c: Vertical(g3)
    c: DistanceX(g2,g1) = 7
    c: DistanceY(g1,g0) = 3
    c: Coincident(g4,g-4)
    c: Coincident(g4,g0)
    c: Coincident(g5,g-3)
    c: Coincident(g5,g0)
    c: Equal(g5,g4)
    c: DistanceY(g0,g4) = 1.5
FEATURE [PartDesign::Pocket] Pocket021  label="POCKET_ElectronicsBox_NutInset"
  BaseFeature = -> Pocket014
  Direction = (0,1,2e-16)
  Length = 10
  Length2 = 5
  Profile = -> Sketch047
  ReferenceAxis = -> Sketch047 [N_Axis]
  Reversed = true
  Type = 0
FEATURE [PartDesign::Mirrored] Mirrored  label="XFORM_ElectronicsBox_NutInsets_X"
  MirrorPlane = -> YZ_Plane027
FEATURE [PartDesign::Mirrored] Mirrored001  label="XFORM_ElectronicsBox_NutInsets_Y"
  MirrorPlane = -> XZ_Plane027
FEATURE [PartDesign::MultiTransform] MultiTransform  label="PAT_ElectronicsBox_NutInsets"
  BaseFeature = -> Pocket021
  Originals = -> [AdditiveLoft,Pocket021,Pocket014]
  Transformations = -> [Mirrored,Mirrored001]
FEATURE [PartDesign::Pad] Pad020  label="PAD_S_ElectronicsBox_HolePads"
  BaseFeature = -> MultiTransform
  Direction = (0,0,1)
  Length = 10
  Length2 = 10
  Profile = -> Sketch035
  ReferenceAxis = -> Sketch035 [N_Axis]
  Type = 0
FEATURE [PartDesign::Pocket] Pocket022  label="POCKET_ElectronicsBox_Holes"
  BaseFeature = -> Pad020
  Direction = (0,0,1)
  Length = 5
  Length2 = 5
  Profile = -> Sketch036
  ReferenceAxis = -> Sketch036 [N_Axis]
  Type = 1
FEATURE [PartDesign::Pocket] Pocket023  label="POCKET_ElectronicsBox_BoltIndent"
  BaseFeature = -> Pocket022
  Direction = (0,0,1)
  Length = 3
  Length2 = 5
  Profile = -> Sketch037
  ReferenceAxis = -> Sketch037 [N_Axis]
  Type = 0
FEATURE [PartDesign::Pocket] Pocket024  label="POCKET_ElectronicsBox_Switches"
  BaseFeature = -> Pocket023
  Direction = (0,1,-2e-16)
  Length = 5
  Length2 = 5
  Profile = -> Sketch038
  ReferenceAxis = -> Sketch038 [N_Axis]
  Type = 0
FEATURE [PartDesign::Pocket] Pocket025  label="POCKET_ElectronicsBox_BackWires"
  BaseFeature = -> Pocket024
  Direction = (0,-1,2e-16)
  Length = 5
  Length2 = 5
  Profile = -> Sketch045
  ReferenceAxis = -> Sketch045 [N_Axis]
  Type = 0
FEATURE [PartDesign::Body] B_ElectronicsBox  label="B_ElectronicsBox_Base"
  Group = -> [Sketch033,Pad016,Sketch034,Sketch035,Sketch036,Sketch037,Sketch038,Sketch039,Pad017,Sketch040,Sketch041,Sketch042,Sketch043,AdditiveLoft,Sketch045,Pocket014,Sketch047,Pocket021,MultiTransform,Mirrored,Mirrored001,Pad020,Pocket022,Pocket023,Pocket024,Pocket025]
  Origin = -> Origin027
  Tip = -> Pocket025
FEATURE [PartDesign::CoordinateSystem] LCS_ElectronicsBox_Fan0
  AttacherType = Attacher::AttachEngine3D
  Placement = pos=(29,37,3) rot=(0,0,1;0rad)
FEATURE [PartDesign::CoordinateSystem] LCA_ElectronicsBox_Fan1
  AttacherType = Attacher::AttachEngine3D
  Placement = pos=(29,-34,3) rot=(0,0,1;0rad)
FEATURE [PartDesign::CoordinateSystem] LCS_ElectronicsBox_Base_Arduino_Hole0
  AttacherType = Attacher::AttachEngine3D
  MapMode = 11
  Placement = pos=(-56,-39,11.5) rot=(0.707107,-0.707107,0;3.14159rad)
FEATURE [PartDesign::CoordinateSystem] LCS_ElectronicsBox_Base_Arduino_Hole1
  AttacherType = Attacher::AttachEngine3D
  MapMode = 11
  Placement = pos=(-56,36.5,11.5) rot=(0.707107,-0.707107,0;3.14159rad)
FEATURE [PartDesign::CoordinateSystem] LCS_ElectronicsBox_Base_Arduino_Hole2
  AttacherType = Attacher::AttachEngine3D
  MapMode = 11
  Placement = pos=(-8,-40.5,11.5) rot=(0.707107,-0.707107,0;3.14159rad)
FEATURE [PartDesign::CoordinateSystem] LCS_ElectronicsBox_Base_Arduino_Hole3
  AttacherType = Attacher::AttachEngine3D
  MapMode = 11
  Placement = pos=(-8,41.5,11.5) rot=(0.707107,-0.707107,0;3.14159rad)
FEATURE [PartDesign::CoordinateSystem] LCS_ElectronicsBox_Base_CNCShield0_Hole0
  AttacherType = Attacher::AttachEngine3D
  MapMode = 11
  Placement = pos=(19.25,-60,11.5) rot=(0.707107,-0.707107,0;3.14159rad)
FEATURE [PartDesign::CoordinateSystem] LCS_ElectronicsBox_Base_CNCShield0_Hole1
  AttacherType = Attacher::AttachEngine3D
  MapMode = 11
  Placement = pos=(19.25,-13,11.5) rot=(0.707107,-0.707107,0;3.14159rad)
FEATURE [PartDesign::CoordinateSystem] LCS_ElectronicsBox_Base_CNCShield1_Hole1
  AttacherType = Attacher::AttachEngine3D
  MapMode = 11
  Placement = pos=(19.25,60,11.5) rot=(0.707107,-0.707107,0;3.14159rad)
FEATURE [PartDesign::CoordinateSystem] LCS_ElectronicsBox_Base_CNCShield1_Hole0
  AttacherType = Attacher::AttachEngine3D
  MapMode = 11
  Placement = pos=(19.25,13,11.5) rot=(0.707107,-0.707107,0;3.14159rad)
FEATURE [PartDesign::CoordinateSystem] LCS_ElectronicsBox_Base_TopHole0
  AttacherType = Attacher::AttachEngine3D
  MapMode = 11
  Placement = pos=(-74,-77,56) rot=(0,0,1;1.5708rad)
FEATURE [PartDesign::CoordinateSystem] LCS_ElectronicsBox_Base_TopHole1
  AttacherType = Attacher::AttachEngine3D
  MapMode = 11
  Placement = pos=(-74,77,56) rot=(0,0,1;1.5708rad)
FEATURE [PartDesign::CoordinateSystem] LCS_ElectronicsBox_Base_TopHole002  label="LCS_ElectronicsBox_Base_TopHole2"
  AttacherType = Attacher::AttachEngine3D
  MapMode = 11
  Placement = pos=(74,-77,56) rot=(0,0,-1;1.5708rad)
FEATURE [PartDesign::CoordinateSystem] LCS_ElectronicsBox_Base_TopHole3
  AttacherType = Attacher::AttachEngine3D
  MapMode = 11
  Placement = pos=(74,77,56) rot=(0,0,-1;1.5708rad)
FEATURE [PartDesign::CoordinateSystem] LCS_ElectronicsBox_Base_Mount0
  AttacherType = Attacher::AttachEngine3D
  MapMode = 11
  Placement = pos=(-90,-58,2) rot=(0,0,1;1.5708rad)
FEATURE [PartDesign::CoordinateSystem] LCS_ElectronicsBox_Base_Mount1
  AttacherType = Attacher::AttachEngine3D
  MapMode = 11
  Placement = pos=(-90,58,2) rot=(0,0,1;1.5708rad)
FEATURE [PartDesign::CoordinateSystem] LCS_ElectronicsBox_Base_Mount2
  AttacherType = Attacher::AttachEngine3D
  MapMode = 11
  Placement = pos=(90,-58,2) rot=(0,0,1;1.5708rad)
FEATURE [PartDesign::CoordinateSystem] LCS_ElectronicsBox_Base_Mount3
  AttacherType = Attacher::AttachEngine3D
  MapMode = 11
  Placement = pos=(90,58,2) rot=(0,0,1;1.5708rad)
FEATURE [PartDesign::CoordinateSystem] LCS_ElectronicsBox_Base_Switch
  AttacherType = Attacher::AttachEngine3D
  Placement = pos=(7.41,-73,35.5) rot=(0,0,1;0rad)
  expr: .Placement.Base.x = <<S_ElectronicsBox_Switches>>.Constraints.SwitchX
  expr: .Placement.Base.z = <<S_ElectronicsBox_Switches>>.Constraints.SwitchY
FEATURE [PartDesign::CoordinateSystem] LCS_ElectronicsBox_Base_USB
  AttacherType = Attacher::AttachEngine3D
  Placement = pos=(-44,-73,23.5) rot=(0,0,1;0rad)
  expr: .Placement.Base.x = -<<S_ElectronicsBox_Switches>>.Constraints.USBX
  expr: .Placement.Base.z = <<S_ElectronicsBox_Switches>>.Constraints.USBY
FEATURE [PartDesign::CoordinateSystem] LCS_ElectronicsBox_Base_PowerCable
  AttacherType = Attacher::AttachEngine3D
  Placement = pos=(-44,73,20) rot=(0,0,1;0rad)
  expr: .Placement.Base.x = -<<S_ElectronicsBox_BackWires>>.Constraints.PowerX
  expr: .Placement.Base.z = <<S_ElectronicsBox_BackWires>>.Constraints.PowerY
FEATURE [App::Part] P_ElectronicsBox  label="P_ElectronicsBox_Base"
  DrawingName = jrobot-electronics-parts.FCStd
  Group = -> [B_ElectronicsBox,LCS_ElectronicsBox_Lid,LCS_Origin006,LCS_ElectronicsBox_Base_Arduino_Hole0,LCS_ElectronicsBox_Base_Arduino_Hole1,LCS_ElectronicsBox_Base_Arduino_Hole2,LCS_ElectronicsBox_Base_Arduino_Hole3,LCS_ElectronicsBox_Base_CNCShield0_Hole0,LCS_ElectronicsBox_Base_CNCShield0_Hole1,LCS_ElectronicsBox_Base_CNCShield1_Hole1,LCS_ElectronicsBox_Base_CNCShield1_Hole0,+11 more]
  Origin = -> Origin026
  PartDescription = B_ElectronicsBox_Base
  PartID = jrobot-electronics-parts
FEATURE [Sketcher::SketchObject] Sketch  label="S_ElectronixBox_Cover_Walls"
  ExternalGeometry = -> [Sketch046]
  FullyConstrained = true
  MapMode = 5
  Support = -> [XY_Plane029]
  sketch-geometry (8):
    g0: LineSegment StartX=85 StartY=-69.8 StartZ=0 EndX=82 EndY=-69.8 EndZ=0
    g1: LineSegment StartX=82 StartY=-69.8 StartZ=0 EndX=82 EndY=69.8 EndZ=0
    g2: LineSegment StartX=82 StartY=69.8 StartZ=0 EndX=85 EndY=69.8 EndZ=0
    g3: LineSegment StartX=85 StartY=69.8 StartZ=0 EndX=85 EndY=-69.8 EndZ=0
    g4: LineSegment StartX=-85 StartY=-69.8 StartZ=0 EndX=-82 EndY=-69.8 EndZ=0
    g5: LineSegment StartX=-82 StartY=-69.8 StartZ=0 EndX=-82 EndY=69.8 EndZ=0
    g6: LineSegment StartX=-82 StartY=69.8 StartZ=0 EndX=-85 EndY=69.8 EndZ=0
    g7: LineSegment StartX=-85 StartY=69.8 StartZ=0 EndX=-85 EndY=-69.8 EndZ=0
  constraints (24):
    c: Coincident(g0,g1)
    c: Coincident(g1,g2)
    c: Coincident(g2,g3)
    c: Coincident(g3,g0)
    c: Horizontal(g0)
    c: Horizontal(g2)
    c: Vertical(g1)
    c: Vertical(g3)
    c: Coincident(g4,g5)
    c: Coincident(g5,g6)
    c: Coincident(g6,g7)
    c: Coincident(g7,g4)
    c: Horizontal(g4)
    c: Horizontal(g6)
    c: Vertical(g5)
    c: Vertical(g7)
    c: Horizontal(g5,g1)
    c: Equal(g4,g0)
    c: Horizontal(g4,g0)
    c: DistanceX(g4,g4) = 3
    c: Vertical(g4,g-3)
    c: Vertical(g0,g-4)
    c: DistanceY(g2,g-6) = 11.2
    c: DistanceY(g-4,g0) = 11.2
FEATURE [PartDesign::Pad] Pad  label="PAD_ElectronixBox_Cover_Walls"
  BaseFeature = -> Pad019
  Direction = (0,0,1)
  Length = 53.6
  Length2 = 10
  Profile = -> Sketch
  ReferenceAxis = -> Sketch [N_Axis]
  Reversed = true
  Type = 0
FEATURE [Sketcher::SketchObject] Sketch048
  AttachmentOffset = pos=(-50,-50,85) rot=(0,0,1;0rad)
  FullyConstrained = true
  MapMode = 5
  Placement = pos=(85,-50,-50) rot=(0.57735,0.57735,0.57735;2.0944rad)
  Support = -> [YZ_Plane029]
  sketch-geometry (4):
    g0: ArcOfCircle CenterX=-10 CenterY=0 CenterZ=0 NormalX=0 NormalY=0 NormalZ=1 AngleXU=0 Radius=1 StartAngle=1.5708 EndAngle=4.71239
    g1: ArcOfCircle CenterX=10 CenterY=0 CenterZ=0 NormalX=0 NormalY=0 NormalZ=1 AngleXU=0 Radius=1 StartAngle=4.71239 EndAngle=7.85398
    g2: LineSegment StartX=-10 StartY=-1 StartZ=0 EndX=10 EndY=-1 EndZ=0
    g3: LineSegment StartX=10 StartY=1 StartZ=0 EndX=-10 EndY=1 EndZ=0
  constraints (9):
    c: Tangent(g0,g2) = -1.5708
    c: Tangent(g2,g1) = -1.5708
    c: Tangent(g1,g3) = -1.5708
    c: Tangent(g3,g0) = -1.5708
    c: Equal(g0,g1)
    c: PointOnObject(g0,g-1)
    c: DistanceY(g0,g0) = 2
    c: Symmetric(g0,g1,g-1)
    c: DistanceX(g0,g1) = 20
FEATURE [PartDesign::Pocket] Pocket
  BaseFeature = -> Pad
  Direction = (-1,2e-16,-3e-16)
  Length = 5
  Length2 = 5
  Profile = -> Sketch048
  ReferenceAxis = -> Sketch048 [N_Axis]
  Type = 0
FEATURE [PartDesign::LinearPattern] LinearPattern
  Direction = -> Sketch048 [H_Axis]
  Length = 100
  Occurrences = 5
FEATURE [PartDesign::LinearPattern] LinearPattern001
  Direction = -> Sketch048 [V_Axis]
  Length = 45
  Occurrences = 8
FEATURE [PartDesign::Mirrored] Mirrored002
  MirrorPlane = -> YZ_Plane029
FEATURE [PartDesign::MultiTransform] MultiTransform001
  BaseFeature = -> Pocket
  Originals = -> [Pocket]
  Transformations = -> [LinearPattern,LinearPattern001,Mirrored002]
FEATURE [PartDesign::Body] Body011  label="B_ElectronicsBox_Cover"
  Group = -> [Sketch046,Pad019,Sketch,Pad,Sketch048,Pocket,MultiTransform001,LinearPattern,LinearPattern001,Mirrored002]
  Origin = -> Origin029
  Tip = -> MultiTransform001
FEATURE [App::Part] P_ElectronicsBox_Cover
  DrawingName = jrobot-electronics-parts.FCStd
  Group = -> [LCS_Origin007,Body011,LCS_ElectronicsBox_Fan0,LCA_ElectronicsBox_Fan1]
  Origin = -> Origin028
  PartDescription = B_ElectronicsBox_Cover
  PartID = jrobot-electronics-parts
FEATURE [App::DocumentObjectGroup] Group011  label="ElectronicsEnclosure"
  Group = -> [P_ElectronicsBox,P_ElectronicsBox_Cover]
FEATURE [App::DocumentObjectGroup] Group007  label="Robot"
  Group = -> [Group011]
FEATURE [App::DocumentObjectGroup] Group  label="Parts"
  Group = -> [Group007]
